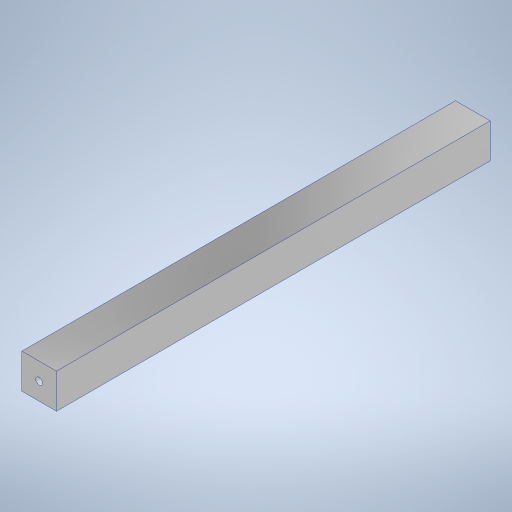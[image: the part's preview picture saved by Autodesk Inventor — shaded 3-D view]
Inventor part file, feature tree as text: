
AUTODESK INVENTOR PART (.ipt)
format: ipt  version: 2024 (Build 280153000, 153)  size: 242,176 bytes
history: native  units: in
note: dims shown in document units (in); Inventor stores cm internally (conversion verified against a paired STEP export)
features: extrude x2, sketch x2
ambient origin geometry x8: Origin, YZ Plane, XZ Plane, XY Plane, X Axis, Y Axis, Z Axis, Center Point
bodies: Solid1 (feature_tree)
feature tree (4):
  extrude  "Extrusion1"  Depth=0.7874in
  extrude  "Extrusion2"  Depth=9.8425in
  sketch  "Sketch1"  dims[d0=0.7874in d1=0.7874in]
  sketch  "Sketch2"  dims[d2=9.8425in d3=0.0in d4=0.1575in d5=0.3937in d6=0.3937in d7=9.8425in d8=0.0in]
